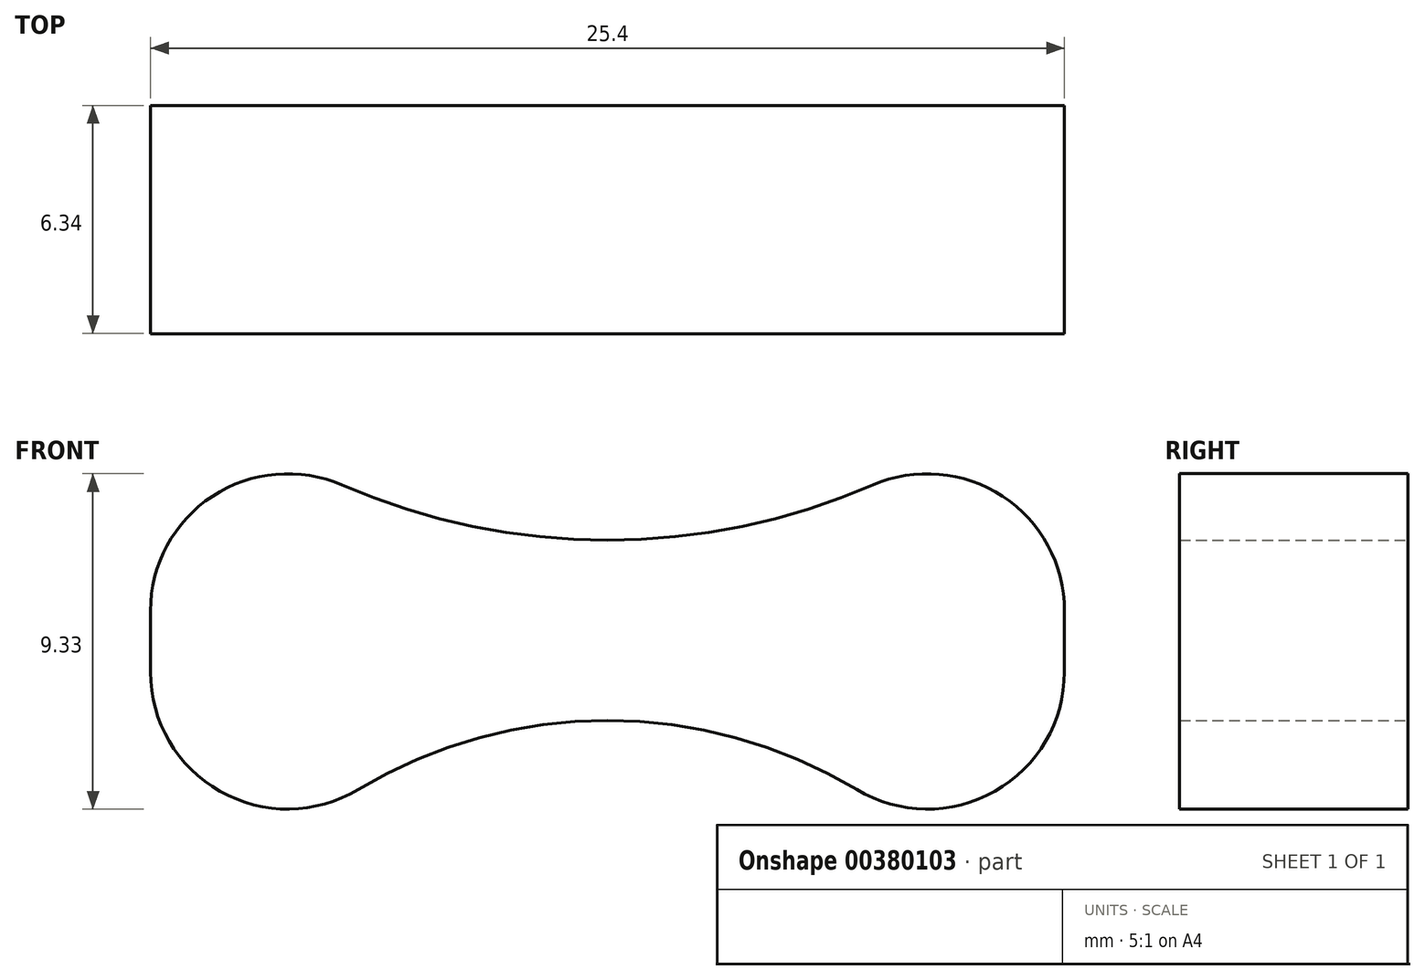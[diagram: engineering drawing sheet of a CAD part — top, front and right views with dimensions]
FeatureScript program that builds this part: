
annotation { "Feature Type Name" : "Feature", "Feature Type Description" : "" }
export const myFeature = defineFeature(function(context is Context, id is Id, definition is map)
    precondition{}
    {
        {
            var Q0;
            Q0=qCreatedBy(makeId("Front.planeOp"),FACE);
            var sketch = newSketch(context, id + "F0", { "sketchPlane" : qUnion([Q0])});
            skLineSegment(sketch, "E0.bottom", {"start": v(-1.76, 14.99) * mm, "end": v(23.64, 14.99) * mm});
            skLineSegment(sketch, "E0.top", {"start": v(-1.76, -4.06) * mm, "end": v(23.64, -4.06) * mm});
            skLineSegment(sketch, "E0.left", {"start": v(-1.76, 14.99) * mm, "end": v(-1.76, -4.06) * mm});
            skLineSegment(sketch, "E0.right", {"start": v(23.64, 14.99) * mm, "end": v(23.64, -4.06) * mm});
            skArc(sketch, "E1", {"start": v(23.64, -4.06) * mm, "mid": v(10.94, 4.93) * mm, "end": v(-1.76, -4.06) * mm});
            skArc(sketch, "E2", {"start": v(-1.76, 14.99) * mm, "mid": v(10.94, 9.95) * mm, "end": v(23.64, 14.99) * mm});
            skSolve(sketch);
        }
        {
            var Q0;
            Q0=makeQuery(id+"F0.imprint","IMPRINT",FACE,{"disambiguationData":[TD([[makeQuery(id+"F0.imprint","IMPRINT",EDGE,{"derivedFrom":sQuery(id+"F0.wireOp",EDGE,"E0.left")}),1.0]])]});
            extrude(context, id + "F1", {"entities" : qUnion([Q0]), "endBound" : BoundingType.SYMMETRIC, "depth" : 6.35 * mm});
        }
        {
            var Q0;
            Q0=makeQuery(id+"F1.opExtrude","SWEPT_EDGE",EDGE,{"disambiguationData":[OSD([sQuery(id+"F0.wireOp",EDGE,"E0.bottom"),sQuery(id+"F0.wireOp",EDGE,"E0.right")])]});
            var Q1;
            Q1=makeQuery(id+"F1.opExtrude","SWEPT_EDGE",EDGE,{"disambiguationData":[OSD([sQuery(id+"F0.wireOp",EDGE,"E0.top"),sQuery(id+"F0.wireOp",EDGE,"E0.right"),sQuery(id+"F0.wireOp",EDGE,"E1")])]});
            var Q2;
            Q2=makeQuery(id+"F1.opExtrude","SWEPT_EDGE",EDGE,{"disambiguationData":[OSD([sQuery(id+"F0.wireOp",EDGE,"E0.top"),sQuery(id+"F0.wireOp",EDGE,"E0.left"),sQuery(id+"F0.wireOp",EDGE,"E1")])]});
            var Q3;
            Q3=makeQuery(id+"F1.opExtrude","SWEPT_EDGE",EDGE,{"disambiguationData":[OSD([sQuery(id+"F0.wireOp",EDGE,"E0.bottom"),sQuery(id+"F0.wireOp",EDGE,"E0.left")])]});
            fillet(context, id + "F2", {"entities" : qUnion([Q0, Q1, Q2, Q3]), "radius" : 3.8 * mm, "tangentPropagation" : true, "allowEdgeOverflow" : false});
        }
    });
